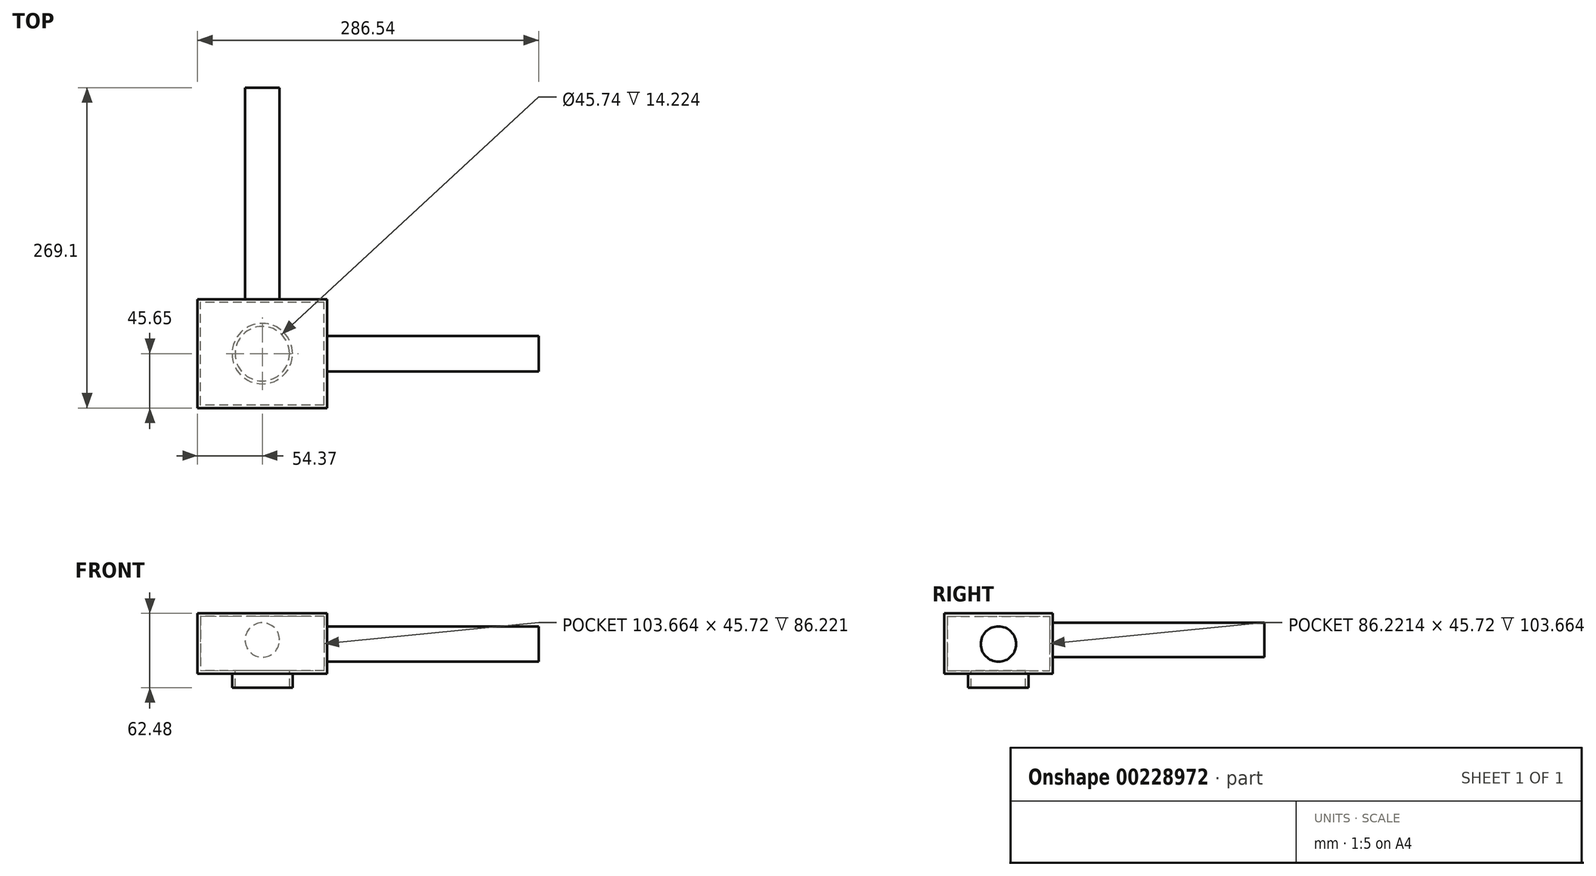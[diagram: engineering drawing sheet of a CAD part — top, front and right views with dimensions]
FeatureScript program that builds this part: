
annotation { "Feature Type Name" : "Feature", "Feature Type Description" : "" }
export const myFeature = defineFeature(function(context is Context, id is Id, definition is map)
    precondition{}
    {
        {
            var Q0;
            Q0=qCreatedBy(makeId("Top.planeOp"),FACE);
            var sketch = newSketch(context, id + "F0", { "sketchPlane" : qUnion([Q0])});
            skLineSegment(sketch, "E0.bottom", {"start": v(54.37, -45.65) * mm, "end": v(-54.37, -45.65) * mm});
            skLineSegment(sketch, "E0.top", {"start": v(54.37, 45.65) * mm, "end": v(-54.37, 45.65) * mm});
            skLineSegment(sketch, "E0.left", {"start": v(54.37, -45.65) * mm, "end": v(54.37, 45.65) * mm});
            skLineSegment(sketch, "E0.right", {"start": v(-54.37, -45.65) * mm, "end": v(-54.37, 45.65) * mm});
            skPoint(sketch, "E0.middle", {"position": v(0, 0) * mm});
            skSolve(sketch);
        }
        {
            var Q0;
            Q0=makeQuery(id+"F0.imprint","IMPRINT",FACE,{"disambiguationData":[TD([[makeQuery(id+"F0.imprint","IMPRINT",EDGE,{"derivedFrom":sQuery(id+"F0.wireOp",EDGE,"E0.bottom")}),-1.0]])]});
            extrude(context, id + "F1", {"entities" : qUnion([Q0]), "depth" : 50.8 * mm});
        }
        {
            var Q0;
            Q0=makeQuery(id+"F1.opExtrude","CAP_FACE",FACE,{"disambiguationData":[OSD([sQuery(id+"F0.wireOp",EDGE,"E0.bottom"),sQuery(id+"F0.wireOp",EDGE,"E0.top"),sQuery(id+"F0.wireOp",EDGE,"E0.left"),sQuery(id+"F0.wireOp",EDGE,"E0.right")])],"isStart":false});
            var sketch = newSketch(context, id + "F2", { "sketchPlane" : qUnion([Q0])});
            skCircle(sketch, "E1", {"center": v(0, 0) * mm, "radius": 25.4 * mm});
            skSolve(sketch);
        }
        {
            var Q0;
            Q0 = qSketchRegion(id + "F2", true);
            extrude(context, id + "F3", {"entities" : qUnion([Q0]), "operationType" : NewBodyOperationType.ADD, "oppositeDirection" : true, "depth" : 62.48 * mm});
        }
        {
            var Q0;
            Q0=makeQuery(id+"F3.opExtrude","CAP_FACE",FACE,{"disambiguationData":[OSD([sQuery(id+"F2.wireOp",EDGE,"E1")])],"isStart":false});
            shell(context, id + "F4", {"entities" : qUnion([Q0]), "thickness" : 2.54 * mm});
        }
        {
            var Q0;
            Q0=makeQuery(id+"F1.opExtrude","SWEPT_FACE",FACE,{"disambiguationData":[OSD([sQuery(id+"F0.wireOp",EDGE,"E0.left")])]});
            var sketch = newSketch(context, id + "F5", { "sketchPlane" : qUnion([Q0])});
            skCircle(sketch, "E2", {"center": v(0, 24.95) * mm, "radius": 14.86 * mm});
            skSolve(sketch);
        }
        {
            var Q0;
            Q0=makeQuery(id+"F5.imprint","IMPRINT",FACE,{"disambiguationData":[TD([[makeQuery(id+"F5.imprint","IMPRINT",EDGE,{"derivedFrom":sQuery(id+"F5.wireOp",EDGE,"E2")}),1.0]])]});
            extrude(context, id + "F6", {"entities" : qUnion([Q0]), "operationType" : NewBodyOperationType.ADD, "depth" : 177.8 * mm});
        }
        {
            var Q0;
            Q0=makeQuery(id+"F1.opExtrude","SWEPT_FACE",FACE,{"disambiguationData":[OSD([sQuery(id+"F0.wireOp",EDGE,"E0.top")])]});
            var sketch = newSketch(context, id + "F7", { "sketchPlane" : qUnion([Q0])});
            skCircle(sketch, "E3", {"center": v(0, 28.32) * mm, "radius": 14.48 * mm});
            skSolve(sketch);
        }
        {
            var Q0;
            Q0=makeQuery(id+"F7.imprint","IMPRINT",FACE,{"disambiguationData":[TD([[makeQuery(id+"F7.imprint","IMPRINT",EDGE,{"derivedFrom":sQuery(id+"F7.wireOp",EDGE,"E3")}),1.0]])]});
            extrude(context, id + "F8", {"entities" : qUnion([Q0]), "operationType" : NewBodyOperationType.ADD, "depth" : 177.8 * mm});
        }
    });
